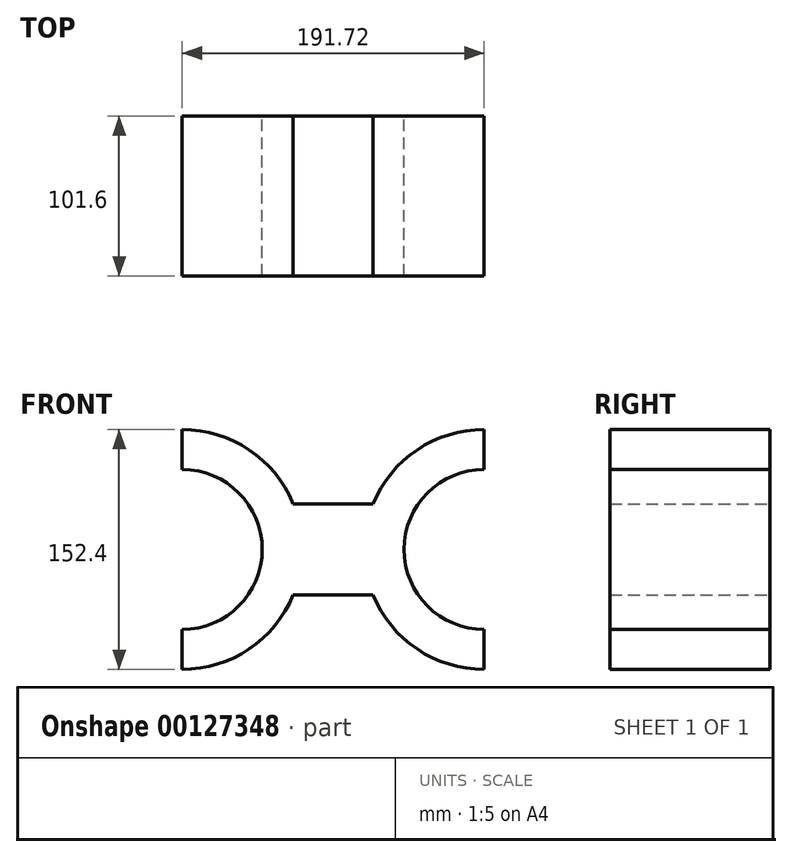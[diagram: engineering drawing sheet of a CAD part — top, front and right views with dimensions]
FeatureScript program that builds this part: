
annotation { "Feature Type Name" : "Feature", "Feature Type Description" : "" }
export const myFeature = defineFeature(function(context is Context, id is Id, definition is map)
    precondition{}
    {
        {
            var Q0;
            Q0=qCreatedBy(makeId("Front.planeOp"),FACE);
            var sketch = newSketch(context, id + "F0", { "sketchPlane" : qUnion([Q0])});
            skLineSegment(sketch, "E0.left", {"start": v(-192, 76.48) * mm, "end": v(-192, 51.08) * mm});
            skLineSegment(sketch, "E0.right", {"start": v(-0.27, 76.48) * mm, "end": v(-0.27, 51.08) * mm});
            skArc(sketch, "E1", {"start": v(-192, -75.92) * mm, "mid": v(-149.57, -63.01) * mm, "end": v(-121.5, -28.67) * mm});
            skArc(sketch, "E2", {"start": v(-0.27, 76.48) * mm, "mid": v(-42.7, 63.58) * mm, "end": v(-70.75, 29.24) * mm});
            skArc(sketch, "E3", {"start": v(-192, -50.52) * mm, "mid": v(-141.2, 0.28) * mm, "end": v(-192, 51.08) * mm});
            skArc(sketch, "E4", {"start": v(-0.27, 51.08) * mm, "mid": v(-51.07, 0.28) * mm, "end": v(-0.27, -50.52) * mm});
            skLineSegment(sketch, "E5.trimOffspring", {"start": v(-192, -50.52) * mm, "end": v(-192, -75.92) * mm});
            skLineSegment(sketch, "E6.trimOffspring", {"start": v(-0.27, -50.52) * mm, "end": v(-0.27, -75.92) * mm});
            skLineSegment(sketch, "E7.bottom", {"start": v(-121.55, 29.36) * mm, "end": v(-70.75, 29.36) * mm});
            skLineSegment(sketch, "E7.top", {"start": v(-121.55, -28.67) * mm, "end": v(-70.75, -28.67) * mm});
            skLineSegment(sketch, "E7.right", {"start": v(-70.75, 29.36) * mm, "end": v(-70.75, 29.24) * mm});
            skArc(sketch, "E8.trimOffspring", {"start": v(-121.55, 29.36) * mm, "mid": v(-149.62, 63.62) * mm, "end": v(-192, 76.48) * mm});
            skArc(sketch, "E9.trimOffspring", {"start": v(-70.75, -28.67) * mm, "mid": v(-42.7, -63.01) * mm, "end": v(-0.27, -75.92) * mm});
            skSolve(sketch);
        }
        {
            var Q0;
            Q0 = qSketchRegion(id + "F0", true);
            extrude(context, id + "F1", {"entities" : qUnion([Q0]), "depth" : 101.6 * mm});
        }
    });
